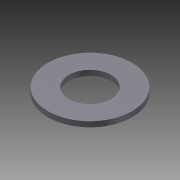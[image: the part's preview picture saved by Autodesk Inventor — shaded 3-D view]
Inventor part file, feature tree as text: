
AUTODESK INVENTOR PART (.ipt)
format: ipt  version: 2012 (Build 160160000, 160)  size: 72,704 bytes
history: native  units: mm
features: extrude x1, sketch x1
ambient origin geometry x8: Origin, YZ Plane, XZ Plane, XY Plane, X Axis, Y Axis, Z Axis, Center Point
bodies: Solid1 (feature_tree)
feature tree (2):
  extrude  "Extrusion1"  Depth=16.0mm
  sketch  "Sketch1"  dims[d0=8.0mm d1=16.0mm d2=1.0mm d3=0.0mm]
